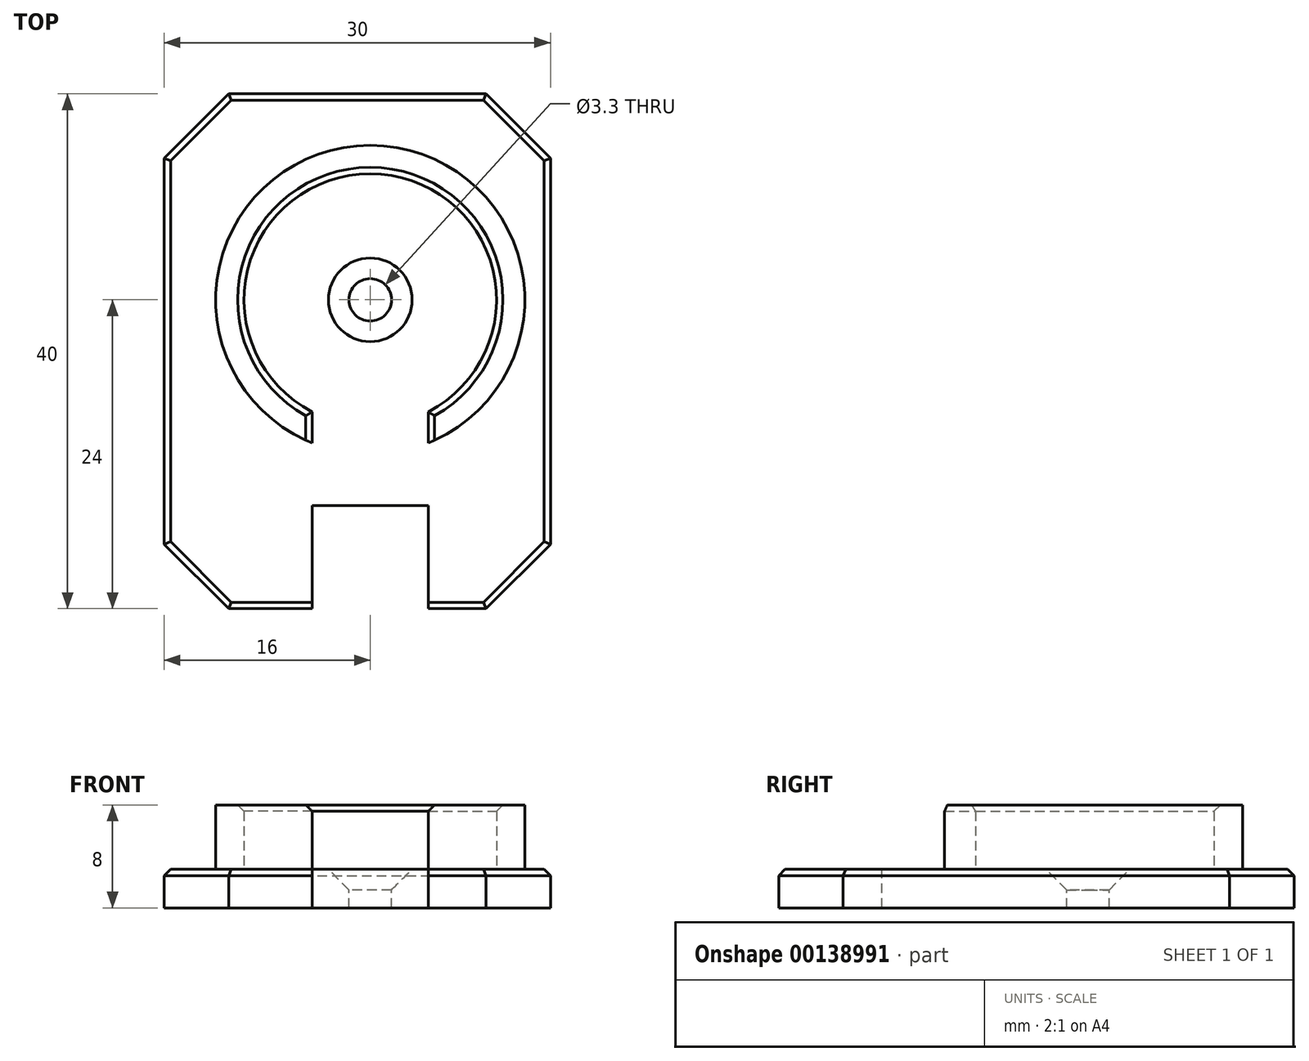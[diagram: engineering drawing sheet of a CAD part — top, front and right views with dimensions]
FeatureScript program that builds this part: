
annotation { "Feature Type Name" : "Feature", "Feature Type Description" : "" }
export const myFeature = defineFeature(function(context is Context, id is Id, definition is map)
    precondition{}
    {
        {
            var Q0;
            Q0=qCreatedBy(makeId("Top.planeOp"),FACE);
            var sketch = newSketch(context, id + "F0", { "sketchPlane" : qUnion([Q0])});
            skCircle(sketch, "E0", {"center": v(0, 0) * mm, "radius": 9.8 * mm});
            skCircle(sketch, "E1", {"center": v(0, 0) * mm, "radius": 12 * mm});
            skLineSegment(sketch, "E2.bottom", {"start": v(-16, 16) * mm, "end": v(14, 16) * mm});
            skLineSegment(sketch, "E2.top", {"start": v(-16, -16) * mm, "end": v(14, -16) * mm});
            skLineSegment(sketch, "E2.left", {"start": v(-16, 16) * mm, "end": v(-16, -16) * mm});
            skLineSegment(sketch, "E2.right", {"start": v(14, 16) * mm, "end": v(14, -16) * mm});
            skLineSegment(sketch, "E3.top", {"start": v(-16, -24) * mm, "end": v(14, -24) * mm});
            skLineSegment(sketch, "E3.left", {"start": v(-16, -16) * mm, "end": v(-16, -24) * mm});
            skLineSegment(sketch, "E3.right", {"start": v(14, -16) * mm, "end": v(14, -24) * mm});
            skLineSegment(sketch, "E4.bottom", {"start": v(-4.5, 0) * mm, "end": v(4.5, 0) * mm});
            skLineSegment(sketch, "E4.top", {"start": v(-4.5, -24) * mm, "end": v(4.5, -24) * mm});
            skLineSegment(sketch, "E4.left", {"start": v(-4.5, 0) * mm, "end": v(-4.5, -24) * mm});
            skLineSegment(sketch, "E4.right", {"start": v(4.5, 0) * mm, "end": v(4.5, -24) * mm});
            skCircle(sketch, "E5", {"center": v(0, 0) * mm, "radius": 1.65 * mm});
            skSolve(sketch);
        }
        {
            var Q0;
            Q0=makeQuery(id+"F0.imprint","IMPRINT",FACE,{"disambiguationData":[TD([[makeQuery(id+"F0.imprint","IMPRINT",EDGE,{"derivedFrom":sQuery(id+"F0.wireOp",EDGE,"E2.bottom")}),-1.0]])]});
            var Q1;
            {var subQ0=sQuery(id+"F0.wireOp",EDGE,"E4.left");var subQ1=sQuery(id+"F0.wireOp",EDGE,"E0");var subQ2=makeQuery(id+"F0.imprint","INTERSECT",VERTEX,{"derivedFrom":[subQ1,subQ0]});Q1=makeQuery(id+"F0.imprint","IMPRINT",FACE,{"disambiguationData":[TD([[makeQuery(id+"F0.imprint","IMPRINT",EDGE,{"disambiguationData":[TD([[subQ2,1.0]])],"derivedFrom":subQ1}),-1.0]])]});}
            var Q2;
            {var subQ5=sQuery(id+"F0.wireOp",EDGE,"E4.bottom");Q2=makeQuery(id+"F0.imprint","IMPRINT",FACE,{"disambiguationData":[TD([[makeQuery(id+"F0.imprint","IMPRINT",EDGE,{"derivedFrom":subQ5}),1.0]])]});}
            var Q3;
            {var subQ5=sQuery(id+"F0.wireOp",EDGE,"E4.bottom");Q3=makeQuery(id+"F0.imprint","IMPRINT",FACE,{"disambiguationData":[TD([[makeQuery(id+"F0.imprint","IMPRINT",EDGE,{"derivedFrom":subQ5}),-1.0]])]});}
            var Q4;
            {var subQ0=sQuery(id+"F0.wireOp",EDGE,"E4.left");var subQ1=sQuery(id+"F0.wireOp",EDGE,"E0");var subQ2=makeQuery(id+"F0.imprint","INTERSECT",VERTEX,{"derivedFrom":[subQ1,subQ0]});Q4=makeQuery(id+"F0.imprint","IMPRINT",FACE,{"disambiguationData":[TD([[makeQuery(id+"F0.imprint","IMPRINT",EDGE,{"disambiguationData":[TD([[subQ2,-1.0]])],"derivedFrom":subQ1}),-1.0]])]});}
            var Q5;
            {var subQ0=sQuery(id+"F0.wireOp",EDGE,"E4.left");var subQ1=sQuery(id+"F0.wireOp",EDGE,"E1");var subQ2=makeQuery(id+"F0.imprint","INTERSECT",VERTEX,{"derivedFrom":[subQ1,subQ0]});Q5=makeQuery(id+"F0.imprint","IMPRINT",FACE,{"disambiguationData":[TD([[makeQuery(id+"F0.imprint","IMPRINT",EDGE,{"disambiguationData":[TD([[subQ2,-1.0]])],"derivedFrom":subQ1}),-1.0]])]});}
            var Q6;
            {var subQ0=sQuery(id+"F0.wireOp",EDGE,"E3.left");Q6=makeQuery(id+"F0.imprint","IMPRINT",FACE,{"disambiguationData":[TD([[makeQuery(id+"F0.imprint","IMPRINT",EDGE,{"derivedFrom":subQ0}),1.0]])]});}
            var Q7;
            {var subQ5=sQuery(id+"F0.wireOp",EDGE,"E4.top");Q7=makeQuery(id+"F0.imprint","IMPRINT",FACE,{"disambiguationData":[TD([[makeQuery(id+"F0.imprint","IMPRINT",EDGE,{"derivedFrom":subQ5}),1.0]])]});}
            var Q8;
            {var subQ0=sQuery(id+"F0.wireOp",EDGE,"E3.right");Q8=makeQuery(id+"F0.imprint","IMPRINT",FACE,{"disambiguationData":[TD([[makeQuery(id+"F0.imprint","IMPRINT",EDGE,{"derivedFrom":subQ0}),-1.0]])]});}
            extrude(context, id + "F1", {"entities" : qUnion([Q0, Q1, Q2, Q3, Q4, Q5, Q6, Q7, Q8]), "oppositeDirection" : true, "depth" : 3 * mm});
        }
        {
            var Q0;
            {var subQ0=sQuery(id+"F0.wireOp",EDGE,"E4.left");var subQ1=sQuery(id+"F0.wireOp",EDGE,"E0");var subQ2=makeQuery(id+"F0.imprint","INTERSECT",VERTEX,{"derivedFrom":[subQ1,subQ0]});Q0=makeQuery(id+"F0.imprint","IMPRINT",FACE,{"disambiguationData":[TD([[makeQuery(id+"F0.imprint","IMPRINT",EDGE,{"disambiguationData":[TD([[subQ2,1.0]])],"derivedFrom":subQ1}),-1.0]])]});}
            extrude(context, id + "F2", {"entities" : qUnion([Q0]), "operationType" : NewBodyOperationType.ADD, "depth" : 5 * mm});
        }
        {
            var Q0;
            Q0=makeQuery(id+"F1.opExtrude","CAP_EDGE",EDGE,{"disambiguationData":[OSD([sQuery(id+"F0.wireOp",EDGE,"E5")])],"isStart":true});
            chamfer(context, id + "F3", {"entities" : qUnion([Q0]), "width" : 1.6 * mm, "tangentPropagation" : true});
        }
        {
            var Q0;
            Q0=makeQuery(id+"F1.opExtrude","SWEPT_EDGE",EDGE,{"disambiguationData":[OSD([sQuery(id+"F0.wireOp",EDGE,"E3.top"),sQuery(id+"F0.wireOp",EDGE,"E3.left")])]});
            var Q1;
            Q1=makeQuery(id+"F1.opExtrude","SWEPT_EDGE",EDGE,{"disambiguationData":[OSD([sQuery(id+"F0.wireOp",EDGE,"E3.top"),sQuery(id+"F0.wireOp",EDGE,"E3.right")])]});
            var Q2;
            Q2=makeQuery(id+"F1.opExtrude","SWEPT_EDGE",EDGE,{"disambiguationData":[OSD([sQuery(id+"F0.wireOp",EDGE,"E2.bottom"),sQuery(id+"F0.wireOp",EDGE,"E2.left")])]});
            var Q3;
            Q3=makeQuery(id+"F1.opExtrude","SWEPT_EDGE",EDGE,{"disambiguationData":[OSD([sQuery(id+"F0.wireOp",EDGE,"E2.bottom"),sQuery(id+"F0.wireOp",EDGE,"E2.right")])]});
            chamfer(context, id + "F4", {"entities" : qUnion([Q0, Q1, Q2, Q3]), "width" : 5 * mm, "tangentPropagation" : true});
        }
        {
            var Q0;
            Q0=makeQuery(id+"F2.opExtrude","CAP_EDGE",EDGE,{"disambiguationData":[OSD([sQuery(id+"F0.wireOp",EDGE,"E0")])],"isStart":false});
            var Q1;
            Q1=makeQuery(id+"F1.opExtrude","CAP_EDGE",EDGE,{"disambiguationData":[OSD([sQuery(id+"F0.wireOp",EDGE,"E3.top"),sQuery(id+"F0.wireOp",EDGE,"E4.top")])],"isStart":true});
            var Q2;
            {var subQ0=sQuery(id+"F0.wireOp",EDGE,"E3.right");var subQ1=sQuery(id+"F0.wireOp",EDGE,"E3.top");Q2=makeQuery(id+"F4.opChamfer","BLEND_EDGE",EDGE,{"blendedFrom":[makeQuery(id+"F1.opExtrude","SWEPT_EDGE",EDGE,{"disambiguationData":[OSD([subQ1,subQ0])]}),makeQuery(id+"F1.opExtrude","CAP_FACE",FACE,{"disambiguationData":[OSD([sQuery(id+"F0.wireOp",EDGE,"E2.bottom"),sQuery(id+"F0.wireOp",EDGE,"E2.left"),sQuery(id+"F0.wireOp",EDGE,"E2.right"),subQ1,sQuery(id+"F0.wireOp",EDGE,"E3.left"),subQ0,sQuery(id+"F0.wireOp",EDGE,"E4.top"),sQuery(id+"F0.wireOp",EDGE,"E5")])],"isStart":true})],"blendedInto":[makeQuery(id+"F1.opExtrude","CAP_FACE",FACE,{"disambiguationData":[OSD([sQuery(id+"F0.wireOp",EDGE,"E2.bottom"),sQuery(id+"F0.wireOp",EDGE,"E2.left"),sQuery(id+"F0.wireOp",EDGE,"E2.right"),subQ1,sQuery(id+"F0.wireOp",EDGE,"E3.left"),subQ0,sQuery(id+"F0.wireOp",EDGE,"E4.top"),sQuery(id+"F0.wireOp",EDGE,"E5")])],"isStart":true})]});}
            var Q3;
            Q3=makeQuery(id+"F1.opExtrude","CAP_EDGE",EDGE,{"disambiguationData":[OSD([sQuery(id+"F0.wireOp",EDGE,"E2.right"),sQuery(id+"F0.wireOp",EDGE,"E3.right")])],"isStart":true});
            var Q4;
            {var subQ0=sQuery(id+"F0.wireOp",EDGE,"E3.left");var subQ1=sQuery(id+"F0.wireOp",EDGE,"E3.top");Q4=makeQuery(id+"F4.opChamfer","BLEND_EDGE",EDGE,{"blendedFrom":[makeQuery(id+"F1.opExtrude","SWEPT_EDGE",EDGE,{"disambiguationData":[OSD([subQ1,subQ0])]}),makeQuery(id+"F1.opExtrude","CAP_FACE",FACE,{"disambiguationData":[OSD([sQuery(id+"F0.wireOp",EDGE,"E2.bottom"),sQuery(id+"F0.wireOp",EDGE,"E2.left"),sQuery(id+"F0.wireOp",EDGE,"E2.right"),subQ1,subQ0,sQuery(id+"F0.wireOp",EDGE,"E3.right"),sQuery(id+"F0.wireOp",EDGE,"E4.top"),sQuery(id+"F0.wireOp",EDGE,"E5")])],"isStart":true})],"blendedInto":[makeQuery(id+"F1.opExtrude","CAP_FACE",FACE,{"disambiguationData":[OSD([sQuery(id+"F0.wireOp",EDGE,"E2.bottom"),sQuery(id+"F0.wireOp",EDGE,"E2.left"),sQuery(id+"F0.wireOp",EDGE,"E2.right"),subQ1,subQ0,sQuery(id+"F0.wireOp",EDGE,"E3.right"),sQuery(id+"F0.wireOp",EDGE,"E4.top"),sQuery(id+"F0.wireOp",EDGE,"E5")])],"isStart":true})]});}
            var Q5;
            Q5=makeQuery(id+"F1.opExtrude","CAP_EDGE",EDGE,{"disambiguationData":[OSD([sQuery(id+"F0.wireOp",EDGE,"E2.left"),sQuery(id+"F0.wireOp",EDGE,"E3.left")])],"isStart":true});
            var Q6;
            {var subQ0=sQuery(id+"F0.wireOp",EDGE,"E2.left");var subQ1=sQuery(id+"F0.wireOp",EDGE,"E2.bottom");Q6=makeQuery(id+"F4.opChamfer","BLEND_EDGE",EDGE,{"blendedFrom":[makeQuery(id+"F1.opExtrude","SWEPT_EDGE",EDGE,{"disambiguationData":[OSD([subQ1,subQ0])]}),makeQuery(id+"F1.opExtrude","CAP_FACE",FACE,{"disambiguationData":[OSD([subQ1,subQ0,sQuery(id+"F0.wireOp",EDGE,"E2.right"),sQuery(id+"F0.wireOp",EDGE,"E3.top"),sQuery(id+"F0.wireOp",EDGE,"E3.left"),sQuery(id+"F0.wireOp",EDGE,"E3.right"),sQuery(id+"F0.wireOp",EDGE,"E4.top"),sQuery(id+"F0.wireOp",EDGE,"E5")])],"isStart":true})],"blendedInto":[makeQuery(id+"F1.opExtrude","CAP_FACE",FACE,{"disambiguationData":[OSD([subQ1,subQ0,sQuery(id+"F0.wireOp",EDGE,"E2.right"),sQuery(id+"F0.wireOp",EDGE,"E3.top"),sQuery(id+"F0.wireOp",EDGE,"E3.left"),sQuery(id+"F0.wireOp",EDGE,"E3.right"),sQuery(id+"F0.wireOp",EDGE,"E4.top"),sQuery(id+"F0.wireOp",EDGE,"E5")])],"isStart":true})]});}
            var Q7;
            Q7=makeQuery(id+"F1.opExtrude","CAP_EDGE",EDGE,{"disambiguationData":[OSD([sQuery(id+"F0.wireOp",EDGE,"E2.bottom")])],"isStart":true});
            var Q8;
            {var subQ0=sQuery(id+"F0.wireOp",EDGE,"E2.right");var subQ1=sQuery(id+"F0.wireOp",EDGE,"E2.bottom");Q8=makeQuery(id+"F4.opChamfer","BLEND_EDGE",EDGE,{"blendedFrom":[makeQuery(id+"F1.opExtrude","SWEPT_EDGE",EDGE,{"disambiguationData":[OSD([subQ1,subQ0])]}),makeQuery(id+"F1.opExtrude","CAP_FACE",FACE,{"disambiguationData":[OSD([subQ1,sQuery(id+"F0.wireOp",EDGE,"E2.left"),subQ0,sQuery(id+"F0.wireOp",EDGE,"E3.top"),sQuery(id+"F0.wireOp",EDGE,"E3.left"),sQuery(id+"F0.wireOp",EDGE,"E3.right"),sQuery(id+"F0.wireOp",EDGE,"E4.top"),sQuery(id+"F0.wireOp",EDGE,"E5")])],"isStart":true})],"blendedInto":[makeQuery(id+"F1.opExtrude","CAP_FACE",FACE,{"disambiguationData":[OSD([subQ1,sQuery(id+"F0.wireOp",EDGE,"E2.left"),subQ0,sQuery(id+"F0.wireOp",EDGE,"E3.top"),sQuery(id+"F0.wireOp",EDGE,"E3.left"),sQuery(id+"F0.wireOp",EDGE,"E3.right"),sQuery(id+"F0.wireOp",EDGE,"E4.top"),sQuery(id+"F0.wireOp",EDGE,"E5")])],"isStart":true})]});}
            var Q9;
            Q9=makeQuery(id+"F2.opExtrude","CAP_EDGE",EDGE,{"disambiguationData":[OSD([sQuery(id+"F0.wireOp",EDGE,"E4.left")])],"isStart":false});
            var Q10;
            Q10=makeQuery(id+"F2.opExtrude","CAP_EDGE",EDGE,{"disambiguationData":[OSD([sQuery(id+"F0.wireOp",EDGE,"E4.right")])],"isStart":false});
            chamfer(context, id + "F5", {"entities" : qUnion([Q0, Q1, Q2, Q3, Q4, Q5, Q6, Q7, Q8, Q9, Q10]), "width" : .5 * mm, "tangentPropagation" : true});
        }
    });
